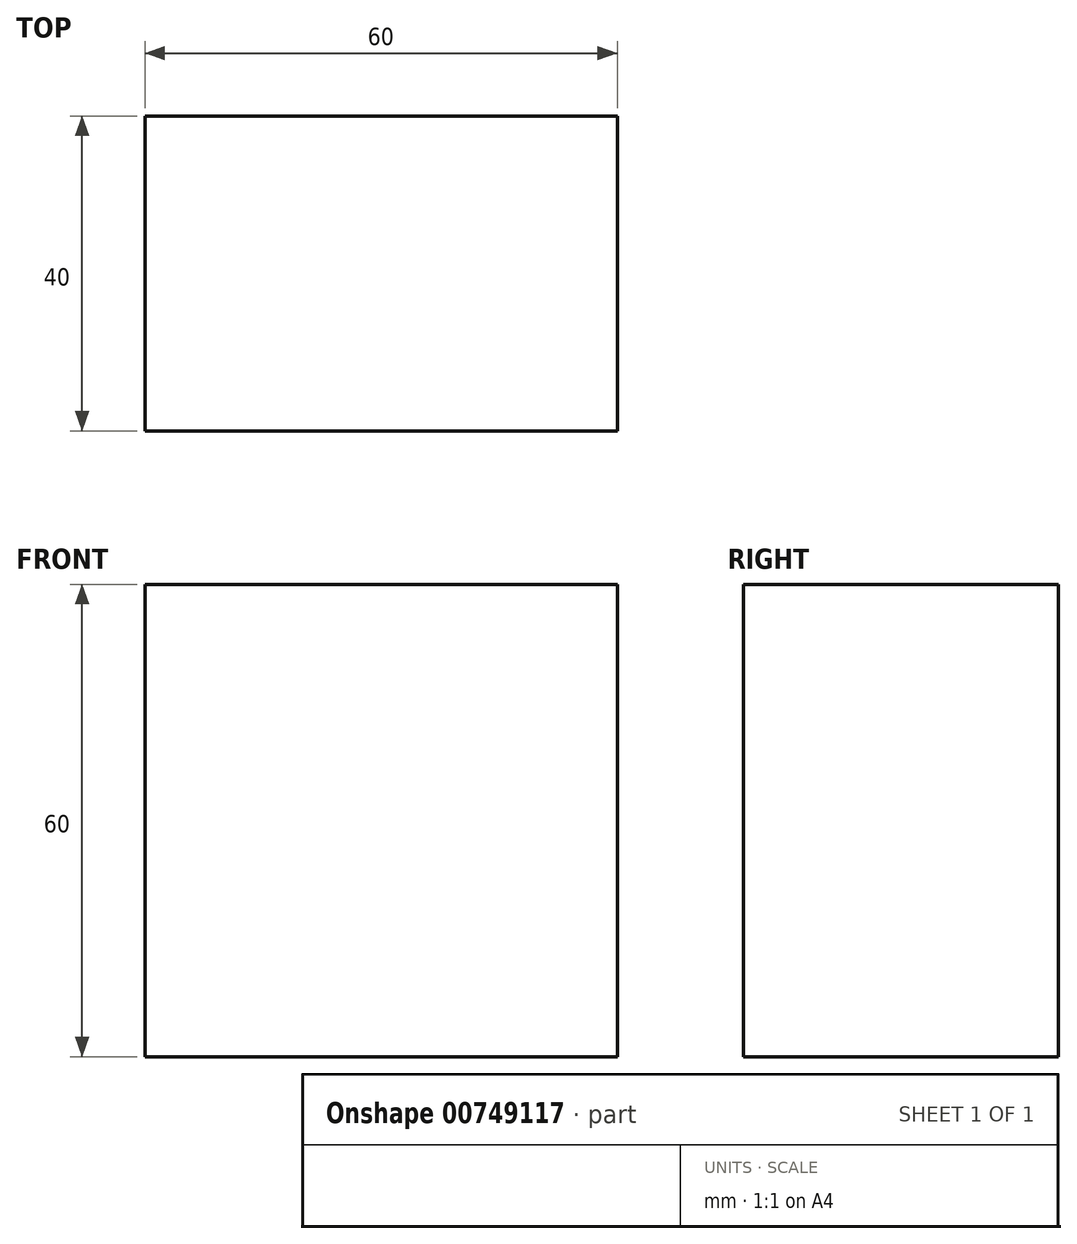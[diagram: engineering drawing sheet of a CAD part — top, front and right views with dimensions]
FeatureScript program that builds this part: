
annotation { "Feature Type Name" : "Feature", "Feature Type Description" : "" }
export const myFeature = defineFeature(function(context is Context, id is Id, definition is map)
    precondition{}
    {
        {
            var Q0;
            Q0=qCreatedBy(makeId("Top.planeOp"),FACE);
            var sketch = newSketch(context, id + "F0", { "sketchPlane" : qUnion([Q0])});
            skLineSegment(sketch, "E0.bottom", {"start": v(0, 40) * mm, "end": v(60, 40) * mm});
            skLineSegment(sketch, "E0.top", {"start": v(0, 0) * mm, "end": v(60, 0) * mm});
            skLineSegment(sketch, "E0.left", {"start": v(0, 40) * mm, "end": v(0, 0) * mm});
            skLineSegment(sketch, "E0.right", {"start": v(60, 40) * mm, "end": v(60, 0) * mm});
            skSolve(sketch);
        }
        {
            var Q0;
            Q0 = qSketchRegion(id + "F0", true);
            extrude(context, id + "F1", {"entities" : qUnion([Q0]), "depth" : 60 * mm, "offsetDistance" : 25 * mm});
        }
    });
